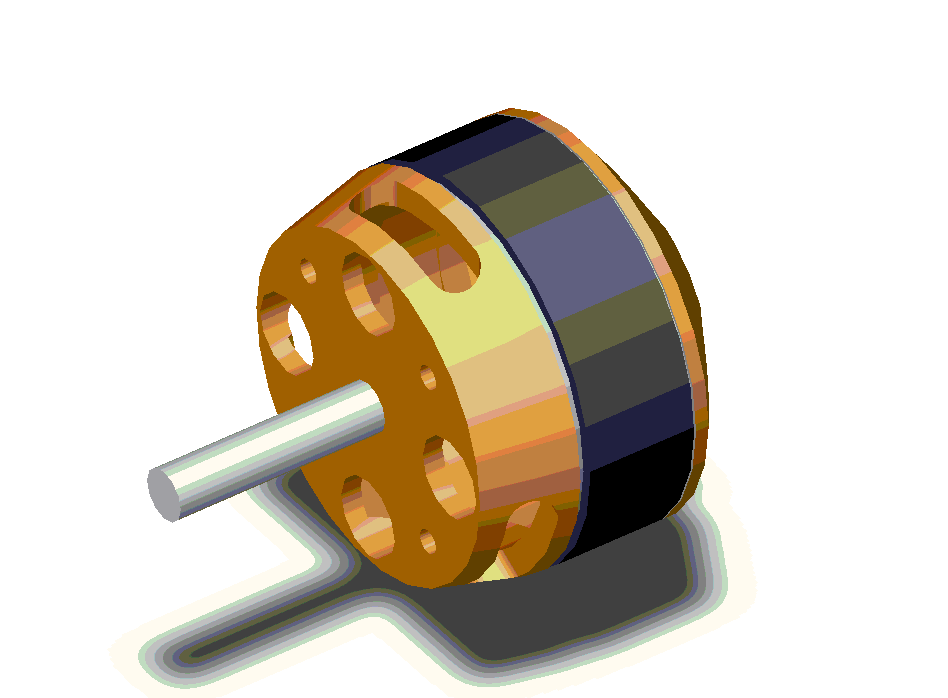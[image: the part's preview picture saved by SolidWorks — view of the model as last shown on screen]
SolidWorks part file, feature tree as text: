
SOLIDWORKS PART (.sldprt)
format: sldprt  version: not decoded by parser v0  size: 214,016 bytes
history: native  units: mm
features: sketch x7, cut_extrude x5, pattern_circular x4, revolve x1, shell x1, extrude x1 (+8 scaffold rows collapsed)
feature tree (27):
  scaffold x8  (default folders/planes/origin — collapsed)
  sketch  "Sketch1"  dims[D1=16.5mm D2=18.68mm D3=27.21mm D4=8.87mm D5=1.0mm D6=1.0mm D7=20.6mm D8=0.25mm D9=0.2mm D10=22.1mm D11=11.35mm D12=29.7mm D13=5.415mm]
  revolve  "Base-Revolve"  Angle=360deg
  shell  "Shell1"  Thickness=2mm
  sketch  "Sketch2"  dims[c1.D1=11.5mm c1.D2=5.75mm c1.D3=2.5mm c1.D4=4.6mm c2.D1=5.75mm c2.D2=11.5mm]
  cut_extrude  "Cut-Extrude1"  [1 undecoded]
  pattern_circular  "CirPattern1"  Count=3 Angle=120deg
  sketch  "Sketch3"  dims[D1=5.0mm]
  cut_extrude  "Cut-Extrude2"  [1 undecoded]
  sketch  "Sketch5"  dims[c1.D1=10.0mm c1.D5=1.58mm c1.D2=10.8mm c1.D3=7.9mm c1.D4=~7.85857mm c2.D4=45.0deg c3.D4=~5.586144mm]
  cut_extrude  "Cut-Extrude3"  Depth=6mm
  pattern_circular  "CirPattern2"  Count=4 Angle=90deg
  sketch  "Sketch6"  dims[D1=7.9mm D2=12.0mm]
  cut_extrude  "Cut-Extrude4"  Depth=6mm
  pattern_circular  "CirPattern3"  Count=4 Angle=90deg
  sketch  "Sketch7"  dims[c1.D1=12.5mm c1.D2=~13.824637mm c2.D2=45.0deg c2.D3=~8.838835mm c2.D4=~8.838835mm]
  cut_extrude  "Cut-Extrude5"  Depth=6mm
  pattern_circular  "CirPattern4"  Count=4 Angle=90deg
  sketch  "Sketch8"  dims[D1=5.0mm]
  extrude  "Boss-Extrude1"  Depth=50.8mm
decode coverage: 17 of 19 modeling features carry decoded parameters
note: ~ marks probable driven/reference dimensions
note: 2 parameter values undecoded
note: suppression state not decoded; provenance and decode notes live in map.json
